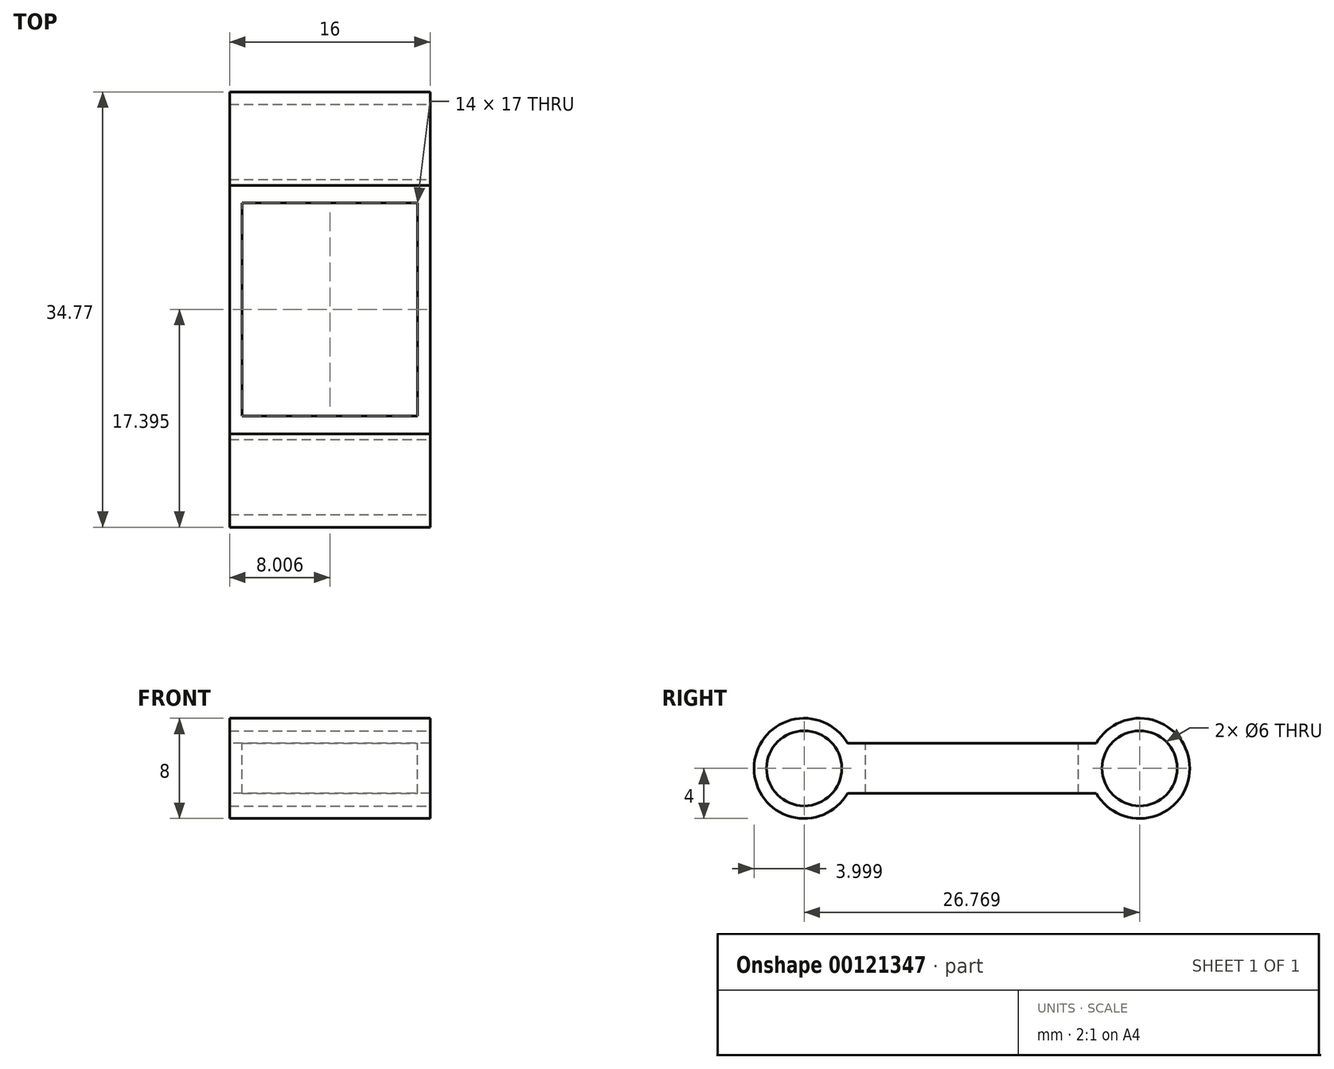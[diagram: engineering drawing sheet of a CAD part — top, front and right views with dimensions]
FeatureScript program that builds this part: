
annotation { "Feature Type Name" : "Feature", "Feature Type Description" : "" }
export const myFeature = defineFeature(function(context is Context, id is Id, definition is map)
    precondition{}
    {
        {
            var Q0;
            Q0=qCreatedBy(makeId("Top.planeOp"),FACE);
            var sketch = newSketch(context, id + "F0", { "sketchPlane" : qUnion([Q0])});
            skLineSegment(sketch, "E0.bottom", {"start": v(-12, -11.81) * mm, "end": v(4, -11.81) * mm});
            skLineSegment(sketch, "E0.top", {"start": v(-12, 8.19) * mm, "end": v(4, 8.19) * mm});
            skLineSegment(sketch, "E0.left", {"start": v(-12, -11.81) * mm, "end": v(-12, 8.19) * mm});
            skLineSegment(sketch, "E0.right", {"start": v(4, -11.81) * mm, "end": v(4, 8.19) * mm});
            skLineSegment(sketch, "E1.bottom", {"start": v(-11, -10.26) * mm, "end": v(3, -10.26) * mm});
            skLineSegment(sketch, "E1.top", {"start": v(-11, 6.74) * mm, "end": v(3, 6.74) * mm});
            skLineSegment(sketch, "E1.left", {"start": v(-11, -10.26) * mm, "end": v(-11, 6.74) * mm});
            skLineSegment(sketch, "E1.right", {"start": v(3, -10.26) * mm, "end": v(3, 6.74) * mm});
            skSolve(sketch);
        }
        {
            var Q0;
            Q0 = qSketchRegion(id + "F0", true);
            extrude(context, id + "F1", {"entities" : qUnion([Q0]), "oppositeDirection" : true, "depth" : 4 * mm});
        }
        {
            var Q0;
            Q0=makeQuery(id+"F1.opExtrude","SWEPT_FACE",FACE,{"disambiguationData":[OSD([sQuery(id+"F0.wireOp",EDGE,"E0.left")])]});
            var sketch = newSketch(context, id + "F2", { "sketchPlane" : qUnion([Q0])});
            skCircle(sketch, "E2", {"center": v(-11.6, -2) * mm, "radius": 4 * mm});
            skPoint(sketch, "E2.centerSnap0", {"position": v(-8.19, -2) * mm});
            skCircle(sketch, "E3", {"center": v(15.16, -2) * mm, "radius": 4 * mm});
            skPoint(sketch, "E3.centerSnap0", {"position": v(11.81, -2) * mm});
            skSolve(sketch);
        }
        {
            var Q0;
            Q0 = qSketchRegion(id + "F2", true);
            extrude(context, id + "F3", {"entities" : qUnion([Q0]), "operationType" : NewBodyOperationType.ADD, "oppositeDirection" : true, "depth" : 16 * mm});
        }
        {
            var Q0;
            Q0=makeQuery(id+"F3.boolean.opBoolean","MERGE",FACE,{"derivedFrom":[makeQuery(id+"F1.opExtrude","SWEPT_FACE",FACE,{"disambiguationData":[OSD([sQuery(id+"F0.wireOp",EDGE,"E0.right")])]}),makeQuery(id+"F3.opExtrude","CAP_FACE",FACE,{"disambiguationData":[OSD([sQuery(id+"F2.wireOp",EDGE,"E2")])],"isStart":false}),makeQuery(id+"F3.opExtrude","CAP_FACE",FACE,{"disambiguationData":[OSD([sQuery(id+"F2.wireOp",EDGE,"E3")])],"isStart":false})]});
            var sketch = newSketch(context, id + "F4", { "sketchPlane" : qUnion([Q0])});
            skCircle(sketch, "E4", {"center": v(-15.16, -2) * mm, "radius": 3 * mm});
            skCircle(sketch, "E5", {"center": v(11.6, -2) * mm, "radius": 3 * mm});
            skSolve(sketch);
        }
        {
            var Q0;
            Q0 = qSketchRegion(id + "F4", true);
            extrude(context, id + "F5", {"entities" : qUnion([Q0]), "operationType" : NewBodyOperationType.REMOVE, "oppositeDirection" : true, "depth" : 16 * mm});
        }
    });
